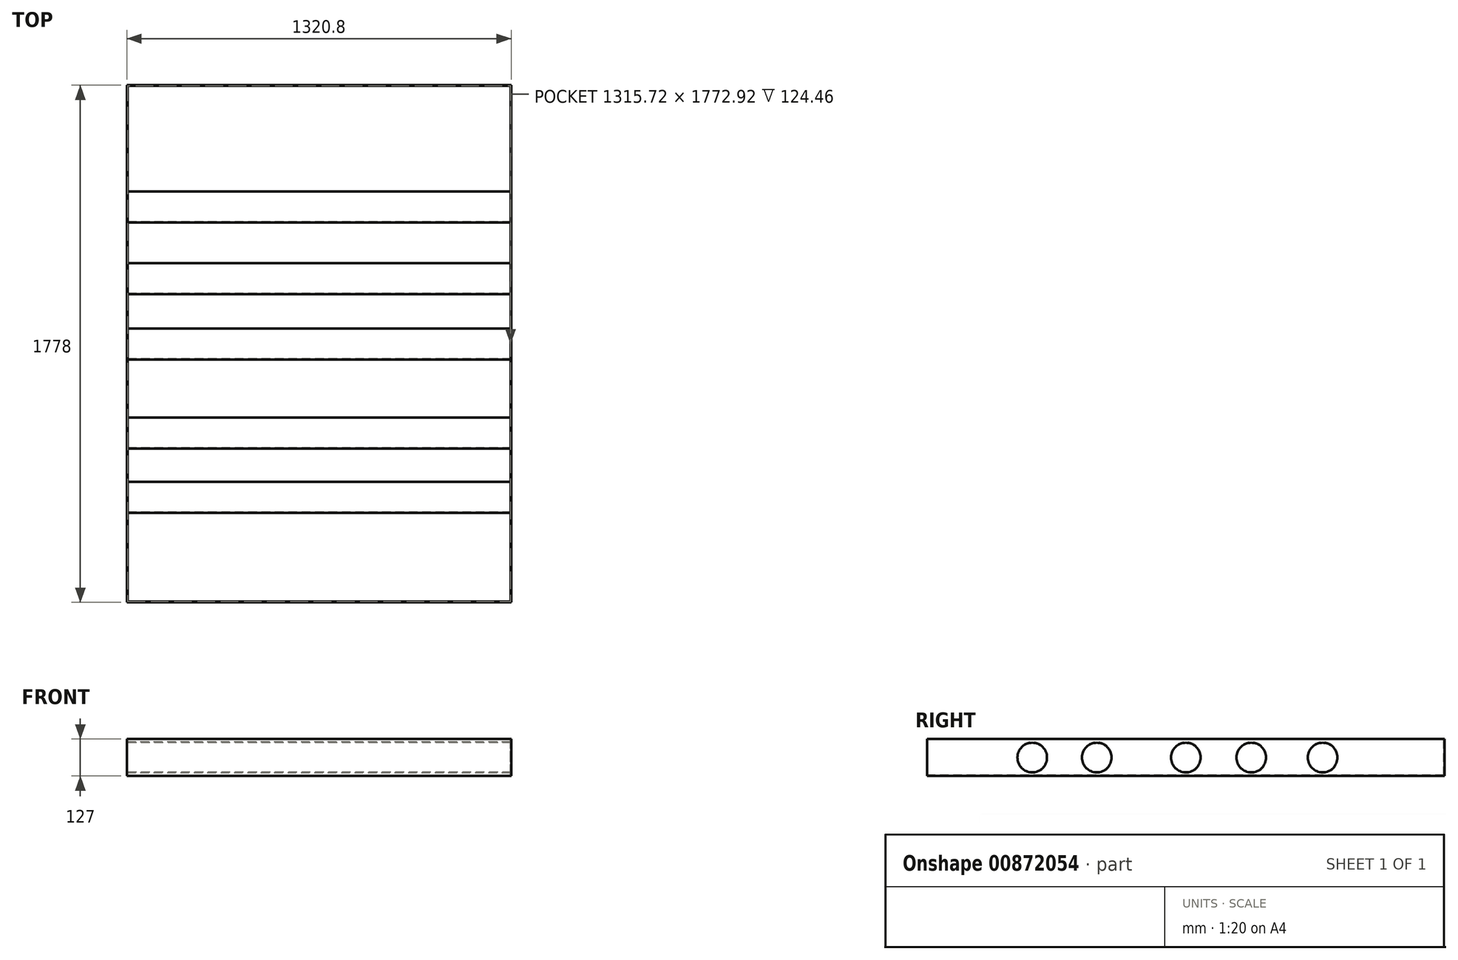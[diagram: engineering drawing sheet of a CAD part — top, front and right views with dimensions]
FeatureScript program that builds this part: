
annotation { "Feature Type Name" : "Feature", "Feature Type Description" : "" }
export const myFeature = defineFeature(function(context is Context, id is Id, definition is map)
    precondition{}
    {
        {
            var Q0;
            Q0=qCreatedBy(makeId("Front.planeOp"),FACE);
            var sketch = newSketch(context, id + "F0", { "sketchPlane" : qUnion([Q0])});
            skLineSegment(sketch, "E0", {"start": v(-1320.8, 127) * mm, "end": v(0, 127) * mm});
            skLineSegment(sketch, "E1", {"start": v(0, 0) * mm, "end": v(0, 127) * mm});
            skLineSegment(sketch, "E2", {"start": v(-1320.8, 0) * mm, "end": v(-1320.8, 127) * mm});
            skLineSegment(sketch, "E3", {"start": v(-1320.8, 0) * mm, "end": v(0, 0) * mm});
            skSolve(sketch);
        }
        {
            var Q0;
            Q0=makeQuery(id+"F0.imprint","IMPRINT",FACE,{"disambiguationData":[TD([[makeQuery(id+"F0.imprint","IMPRINT",EDGE,{"derivedFrom":sQuery(id+"F0.wireOp",EDGE,"E0")}),-1.0]])]});
            extrude(context, id + "F1", {"entities" : qUnion([Q0]), "oppositeDirection" : true, "depth" : 1778 * mm, "offsetDistance" : 25.4 * mm});
        }
        {
            var Q0;
            Q0=makeQuery(id+"F1.opExtrude","SWEPT_FACE",FACE,{"disambiguationData":[OSD([sQuery(id+"F0.wireOp",EDGE,"E2")])]});
            var sketch = newSketch(context, id + "F2", { "sketchPlane" : qUnion([Q0])});
            skLineSegment(sketch, "E4", {"start": v(-1524, 63.5) * mm, "end": v(-254, 63.5) * mm, "construction": true});
            skLineSegment(sketch, "E5", {"start": v(-889, 127) * mm, "end": v(-889, 0) * mm, "construction": true});
            skCircle(sketch, "E6", {"center": v(-1358.69, 63.5) * mm, "radius": 50.8 * mm});
            skCircle(sketch, "E7", {"center": v(-888.52, 63.5) * mm, "radius": 50.8 * mm});
            skCircle(sketch, "E8", {"center": v(-360.66, 63.5) * mm, "radius": 50.8 * mm});
            skCircle(sketch, "E9", {"center": v(-582.46, 63.5) * mm, "radius": 50.8 * mm});
            skCircle(sketch, "E10", {"center": v(-1113.46, 63.5) * mm, "radius": 50.8 * mm});
            skSolve(sketch);
        }
        {
            var Q0;
            Q0 = qSketchRegion(id + "F2", true);
            extrude(context, id + "F3", {"entities" : qUnion([Q0]), "operationType" : NewBodyOperationType.REMOVE, "oppositeDirection" : true, "depth" : 1465.58 * mm, "offsetDistance" : 25.4 * mm});
        }
        {
            var Q0;
            Q0=makeQuery(id+"F1.opExtrude","SWEPT_FACE",FACE,{"disambiguationData":[OSD([sQuery(id+"F0.wireOp",EDGE,"E0")])]});
            shell(context, id + "F4", {"entities" : qUnion([Q0]), "thickness" : 2.54 * mm});
        }
    });
